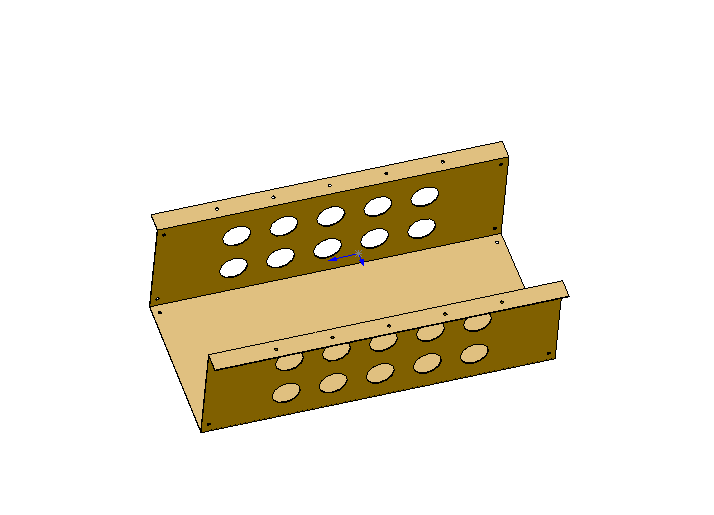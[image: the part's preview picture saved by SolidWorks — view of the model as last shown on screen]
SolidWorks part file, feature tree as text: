
SOLIDWORKS PART (.sldprt)
format: sldprt  version: not decoded by parser v0  size: 885,248 bytes
history: native  units: mm
features: sketch x8, extrude x2, hole x2, shell x1, sheet_metal_op x1 (+10 scaffold rows collapsed)
feature tree (24):
  scaffold x10  (default folders/planes/origin — collapsed)
  sketch  "Sketch1"  dims[c1.D1=50.8mm c1.D2=50.8mm c2.D1=12.7mm c2.D2=12.7mm]
  extrude  "Extrude1"  [1 undecoded]
  shell  "Shell1"  Thickness=1.27mm
  sketch  "Sketch27"  dims[D1=1.27mm D2=1.27mm]
  extrude  "Extrude4"  [1 undecoded]
  hole  "#6 Clearance Hole1"  Diameter=4.3053mm Depth=1.27mm
  sketch  "Sketch35"
  sketch  "Sketch34"  dims[c1.D1=25.4mm c1.D2=93.98mm c1.4=25.4mm c1.D4=19.05mm c1.D7=33.02mm c1.D5=25.4mm c1.D3=50.8mm c1.D6=31.75mm c2.D5=58.42mm c2.D7=~8.980256mm c3.D7=90.0deg c3.D6=~2059.488517mm c3.D8=~8.980256mm c4.D8=~2059.488517mm c4.D9=~17.960512mm c5.D9=~2059.488517mm c5.D3=50.8mm c5.D4=31.75mm c5.D5=58.42mm c5.D6=~4.444873mm c6.D6=~2094.395102mm c6.D7=33.02mm c6.D8=~4.444873mm c7.D8=~1570.796327mm c7.D9=~14.816244mm c8.D9=~2059.488517mm c8.D1=12.7mm c8.D2=93.98mm c8.D3=25.4mm c9.D1=114.3mm c10.D1=~2356.19449mm c11.D1=25.4mm c11.D2=93.98mm c11.D3=50.8mm c11.D4=~17.960512mm c12.D4=~1431.169987mm c12.D5=~14.816244mm c13.D5=~2059.488517mm c13.D6=12.7mm c13.D1=25.4mm c13.D2=93.98mm c13.D3=31.75mm c13.D4=~33.297463mm c14.D4=~2094.395102mm c14.D5=~14.816244mm c15.D5=~2059.488517mm c15.D1=25.4mm c15.D2=101.6mm c15.D3=31.75mm c15.D4=~3.666174mm c16.D4=~2094.395102mm c16.D5=30.48mm c16.D6=~9.919017mm c17.D6=~2059.488517mm c17.D1=25.4mm c17.D2=101.6mm c17.D3=31.75mm c17.D4=~3.666174mm c18.D4=~2094.395102mm c18.Thru Hole Dia.=4.3053mm c18.Thru Hole Depth=1.27mm]
  hole  "5/16 Clearance Hole1"  Diameter=8.72998mm Depth=1.27mm
  sketch  "Sketch39"
  sketch  "Sketch38"  dims[hole-wizard template sketch: 54 standard entries collapsed; hole parameters kept: c17.D1=25.4mm c17.D2=101.6mm c17.D3=31.75mm c17.D4=~3.666174mm c18.D4=~2094.395102mm c18.Thru Hole Dia.=~8.72998mm c18.Thru Hole Depth=1.27mm]
  sheet_metal_op  "Sheet-Metal3"  Thickness=1.27mm
  sketch  "Sharp-Sketch3"  dims[c1.SharpBend43=0.0 c1.D1=0.0mm c1.D4=~1261.261268mm c1.D5=2.0 c1.D8=~0.036383deg c1.D9=~0.036383deg c1.SharpBend45=0.0 c2.D1=0.0mm c2.D4=~1260.881308mm c2.D5=4.0 c2.D8=~0.036383deg c2.D9=~0.036383deg c2.SharpBend46=0.0 c3.D1=0.0mm c3.D4=~1261.261268mm c3.D5=3.0 c3.D8=~0.036383deg c3.D9=~0.036383deg c4.D1=0.0mm c4.D4=~1260.881308mm c4.D5=1.0 c4.D8=~0.036383deg c4.D9=~0.036383deg]
  sketch  "Flat-Sketch3"  dims[D1=0.0mm]
decode coverage: 10 of 14 modeling features carry decoded parameters
note: ~ marks probable driven/reference dimensions
note: 2 parameter values undecoded
note: suppression state not decoded; provenance and decode notes live in map.json
